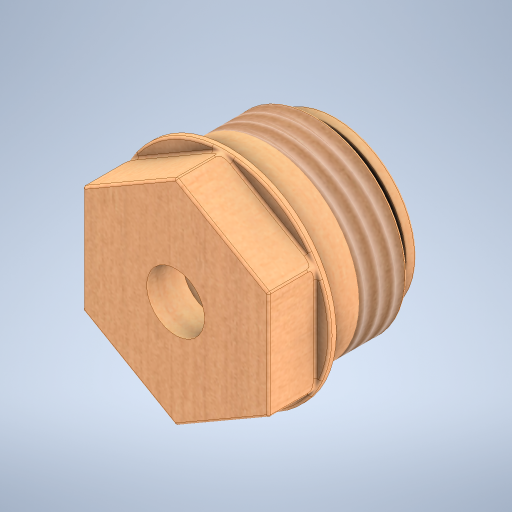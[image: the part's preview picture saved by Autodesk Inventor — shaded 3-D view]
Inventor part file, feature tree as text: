
AUTODESK INVENTOR PART (.ipt)
format: ipt  version: 2024 (Build 280153000, 153)  size: 636,928 bytes
history: native  units: in
note: dims shown in document units (in); Inventor stores cm internally (conversion verified against a paired STEP export)
features: sketch x6, extrude x4, fillet x2, projected_geometry x2, pattern_circular x1, revolve x1, thread x1, hole x1, direct_edit x1, other x1
ambient origin geometry x8: Origin, YZ Plane, XZ Plane, XY Plane, X Axis, Y Axis, Z Axis, Center Point
bodies: Solid1 (feature_tree)
feature tree (20):
  extrude  "Extrusion1"  Depth=0.5in TaperAngle=0.0deg
  extrude  "Extrusion2"  Depth=2.3622in TaperAngle=360.0deg
  pattern_circular  "Circular Pattern1"  [2 undecoded]
  fillet  "Fillet1"  Radius=0.05in
  extrude  "Extrusion3"  Depth=0.3937in
  extrude  "Extrusion4"  Depth=0.3937in
  revolve  "Revolution1"  [1 undecoded]
  fillet  "Fillet2"  [1 undecoded]
  thread  "Thread1"  [1 undecoded]
  hole  "Hole2"  [1 undecoded]
  direct_edit  "Direct Edit1"
  sketch  "Sketch1"  dims[d0=0.5in d1=0.125in d2=0.0in]
  sketch  "Sketch2"  dims[d3=0.11in d4=0.0in d5=2.3622in d6=360.0deg]
  projected_geometry  "Projected Loop1"
  sketch  "Sketch3"  dims[d8=0.005in]
  sketch  "Sketch4"  dims[d9=0.43in]
  sketch  "Sketch6"  dims[d10=0.25in d11=0.0in]
  sketch  "Sketch7"  dims[d12=0.25in d13=0.29in d14=0.0in d22=0.05in d23=0.025in d24=0.025in d25=0.375in d26=90.0deg d27=0.005in d28=1.0236in d29=0.0in d30=0.135in d31=0.75in d32=0.375in d33=0.25in d34=0.5635in d35=1.0in d36=0.8108in d37=3.937in d38=0.3937in d39=0.3937in]
  projected_geometry  "Project Cut Edges1"
  other  "Scale1"
note: 6 required parameter values undecoded (feature->parameter linkage not recoverable at this tier; creation-order binding heuristic only, values carry confidence <= 0.55)